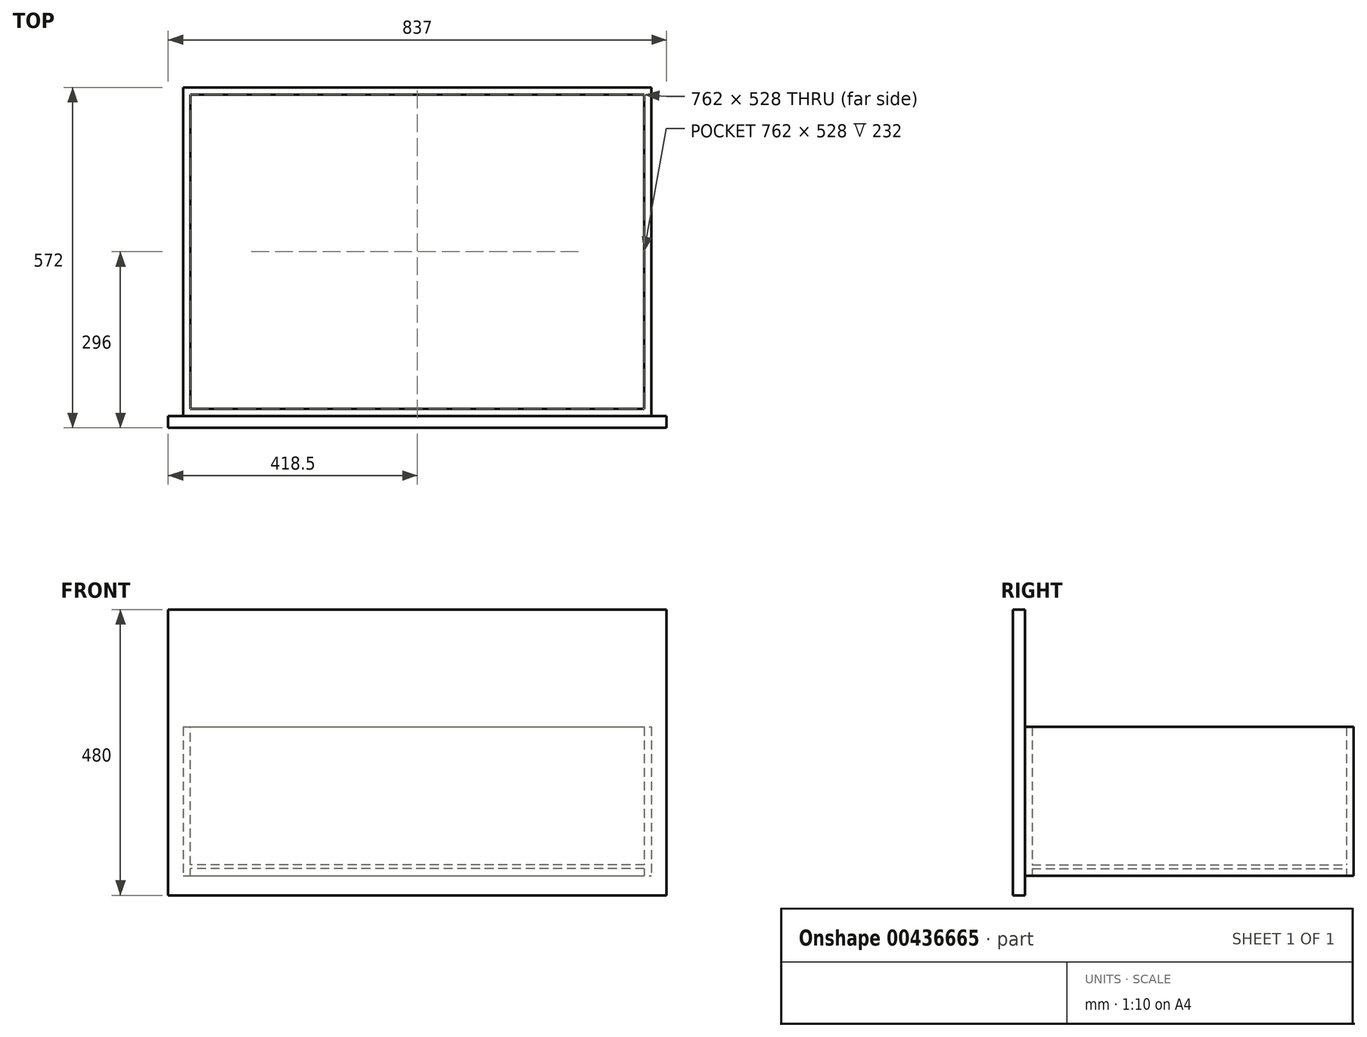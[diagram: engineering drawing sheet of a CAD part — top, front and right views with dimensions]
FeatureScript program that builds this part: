
annotation { "Feature Type Name" : "Feature", "Feature Type Description" : "" }
export const myFeature = defineFeature(function(context is Context, id is Id, definition is map)
    precondition{}
    {
        {
            var Q0;
            Q0=qCreatedBy(makeId("Front.planeOp"),FACE);
            var sketch = newSketch(context, id + "F0", { "sketchPlane" : qUnion([Q0])});
            skLineSegment(sketch, "E0.bottom", {"start": v(381, 3) * mm, "end": v(-381, 3) * mm});
            skLineSegment(sketch, "E0.top", {"start": v(381, -3) * mm, "end": v(-381, -3) * mm});
            skPoint(sketch, "E0.middle", {"position": v(0, 0) * mm});
            skLineSegment(sketch, "E1.bottom", {"start": v(-381, 235) * mm, "end": v(-393, 235) * mm});
            skLineSegment(sketch, "E1.top", {"start": v(-381, -15) * mm, "end": v(-393, -15) * mm});
            skLineSegment(sketch, "E1.left", {"start": v(-381, 235) * mm, "end": v(-381, 3) * mm});
            skLineSegment(sketch, "E1.right", {"start": v(-393, 235) * mm, "end": v(-393, -15) * mm});
            skLineSegment(sketch, "E2.bottom", {"start": v(381, 235) * mm, "end": v(393, 235) * mm});
            skLineSegment(sketch, "E2.top", {"start": v(381, -15) * mm, "end": v(393, -15) * mm});
            skLineSegment(sketch, "E2.left", {"start": v(381, 235) * mm, "end": v(381, 3) * mm});
            skLineSegment(sketch, "E2.right", {"start": v(393, 235) * mm, "end": v(393, -15) * mm});
            skLineSegment(sketch, "E3.trimOffspring", {"start": v(-381, -3) * mm, "end": v(-381, -15) * mm});
            skLineSegment(sketch, "E4.trimOffspring", {"start": v(381, -3) * mm, "end": v(381, -15) * mm});
            skSolve(sketch);
        }
        {
            var Q0;
            Q0=qSketchRegion(id+"F0",true);
            extrude(context, id + "F1", {"entities" : qUnion([Q0]), "depth" : 552 * mm});
        }
        {
            var Q0;
            Q0=makeQuery(id+"F1.opExtrude","SWEPT_FACE",FACE,{"disambiguationData":[OSD([sQuery(id+"F0.wireOp",EDGE,"E2.left")])]});
            var sketch = newSketch(context, id + "F2", { "sketchPlane" : qUnion([Q0])});
            skLineSegment(sketch, "E5.bottom", {"start": v(0, 235) * mm, "end": v(12, 235) * mm});
            skLineSegment(sketch, "E5.top", {"start": v(0, -15) * mm, "end": v(12, -15) * mm});
            skLineSegment(sketch, "E5.left", {"start": v(0, 235) * mm, "end": v(0, -15) * mm});
            skLineSegment(sketch, "E5.right", {"start": v(12, 235) * mm, "end": v(12, -15) * mm});
            skLineSegment(sketch, "E6.bottom", {"start": v(552, 235) * mm, "end": v(540, 235) * mm});
            skLineSegment(sketch, "E6.top", {"start": v(552, -15) * mm, "end": v(540, -15) * mm});
            skLineSegment(sketch, "E6.left", {"start": v(552, 235) * mm, "end": v(552, -15) * mm});
            skLineSegment(sketch, "E6.right", {"start": v(540, 235) * mm, "end": v(540, -15) * mm});
            skSolve(sketch);
        }
        {
            var Q0;
            Q0=qSketchRegion(id+"F2",true);
            var Q1;
            Q1=makeQuery(id+"F1.opExtrude","SWEPT_FACE",FACE,{"disambiguationData":[OSD([sQuery(id+"F0.wireOp",EDGE,"E1.left")])]});
            extrude(context, id + "F3", {"entities" : qUnion([Q0]), "operationType" : NewBodyOperationType.ADD, "endBound" : BoundingType.UP_TO_SURFACE, "endBoundEntityFace" : qUnion([Q1]), "depth" : 520 * mm});
        }
        {
            var Q0;
            Q0=makeQuery(id+"F1.opExtrude","CAP_FACE",FACE,{"disambiguationData":[OSD([sQuery(id+"F0.wireOp",EDGE,"E0.bottom"),sQuery(id+"F0.wireOp",EDGE,"E0.top"),sQuery(id+"F0.wireOp",EDGE,"E1.bottom"),sQuery(id+"F0.wireOp",EDGE,"E1.top"),sQuery(id+"F0.wireOp",EDGE,"E1.left"),sQuery(id+"F0.wireOp",EDGE,"E1.right"),sQuery(id+"F0.wireOp",EDGE,"E2.bottom"),sQuery(id+"F0.wireOp",EDGE,"E2.top"),sQuery(id+"F0.wireOp",EDGE,"E2.left"),sQuery(id+"F0.wireOp",EDGE,"E2.right"),sQuery(id+"F0.wireOp",EDGE,"E3.trimOffspring"),sQuery(id+"F0.wireOp",EDGE,"E4.trimOffspring")])],"isStart":false});
            var sketch = newSketch(context, id + "F4", { "sketchPlane" : qUnion([Q0])});
            skLineSegment(sketch, "E7.bottom", {"start": v(-418.5, 432) * mm, "end": v(418.5, 432) * mm});
            skLineSegment(sketch, "E7.top", {"start": v(-418.5, -48) * mm, "end": v(418.5, -48) * mm});
            skLineSegment(sketch, "E7.left", {"start": v(-418.5, 432) * mm, "end": v(-418.5, -48) * mm});
            skLineSegment(sketch, "E7.right", {"start": v(418.5, 432) * mm, "end": v(418.5, -48) * mm});
            skSolve(sketch);
        }
        {
            var Q0;
            Q0=qSketchRegion(id+"F4",true);
            extrude(context, id + "F5", {"entities" : qUnion([Q0]), "operationType" : NewBodyOperationType.ADD, "depth" : 20 * mm});
        }
    });
